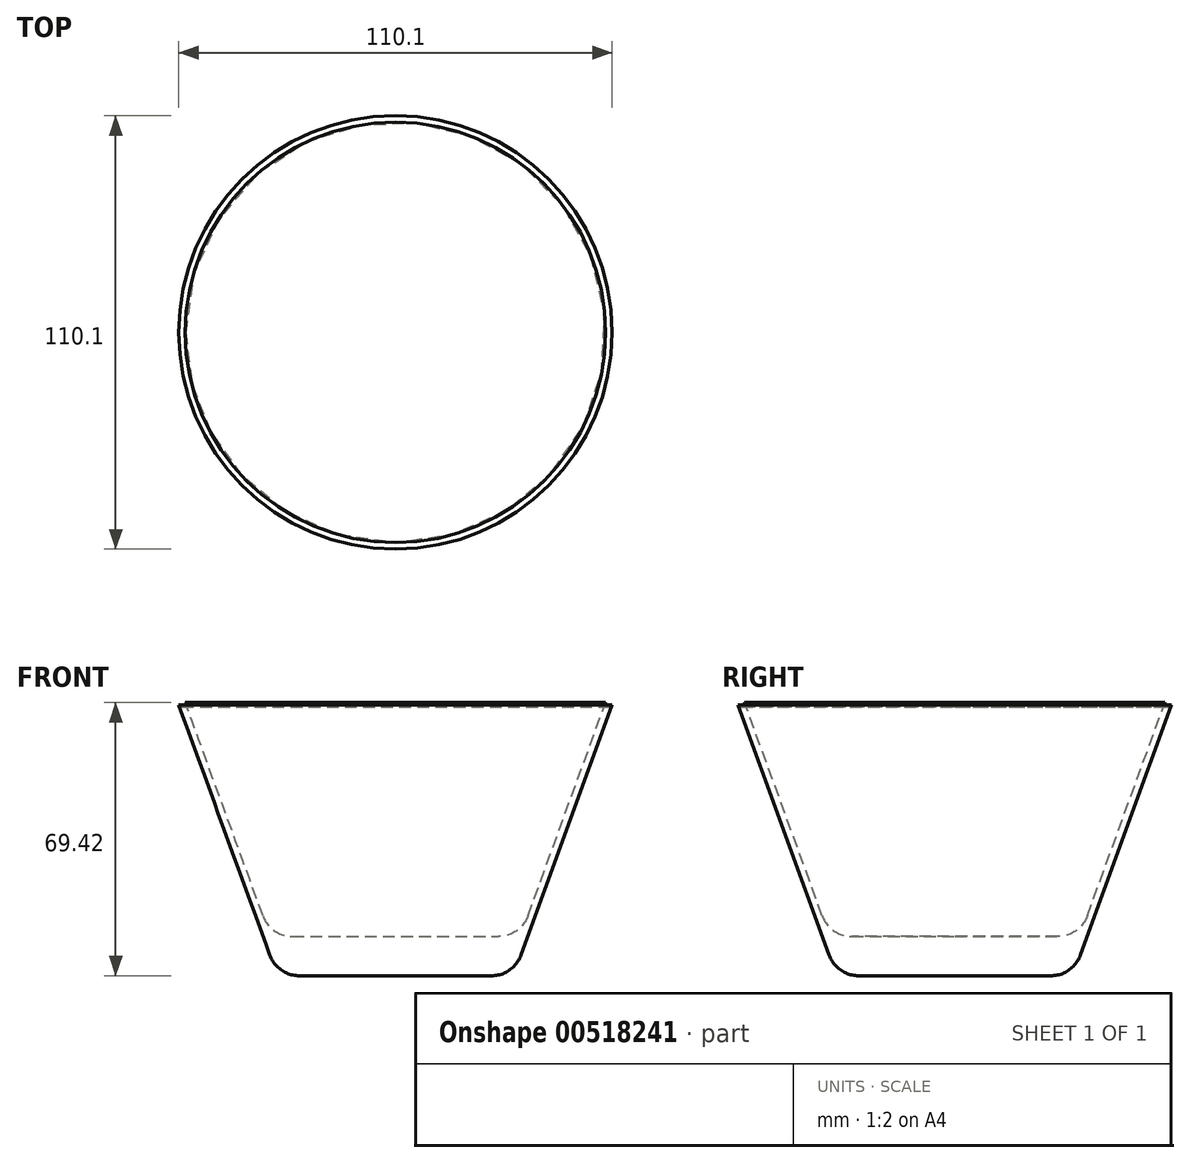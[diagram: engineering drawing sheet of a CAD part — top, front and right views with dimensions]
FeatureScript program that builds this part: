
annotation { "Feature Type Name" : "Feature", "Feature Type Description" : "" }
export const myFeature = defineFeature(function(context is Context, id is Id, definition is map)
    precondition{}
    {
        {
            var Q0;
            Q0=qCreatedBy(makeId("Front.planeOp"),FACE);
            var sketch = newSketch(context, id + "F0", { "sketchPlane" : qUnion([Q0])});
            skLineSegment(sketch, "E0", {"start": v(0, 0) * mm, "end": v(24.4, 0) * mm});
            skLineSegment(sketch, "E1", {"start": v(31.92, 5.26) * mm, "end": v(55.05, 68.83) * mm});
            skPoint(sketch, "E2.visualSharp", {"position": v(30, 0) * mm});
            skArc(sketch, "E2.filletArc", {"start": v(24.4, 0) * mm, "mid": v(28.99, 1.45) * mm, "end": v(31.92, 5.26) * mm});
            skLineSegment(sketch, "E3.0", {"start": v(33.7, 15.26) * mm, "end": v(53.4, 69.42) * mm});
            skLineSegment(sketch, "E4", {"start": v(0, 10) * mm, "end": v(26.18, 10) * mm});
            skArc(sketch, "E5.filletArc", {"start": v(26.18, 10) * mm, "mid": v(30.76, 11.45) * mm, "end": v(33.7, 15.26) * mm});
            skCircle(sketch, "E6", {"center": v(54.23, 69.12) * mm, "radius": 0.88 * mm});
            skPoint(sketch, "E6.first.point", {"position": v(53.4, 69.42) * mm});
            skPoint(sketch, "E6.second.point", {"position": v(54.23, 70) * mm});
            skPoint(sketch, "E6.third.point", {"position": v(55.05, 68.83) * mm});
            skLineSegment(sketch, "E7", {"start": v(0, 0) * mm, "end": v(0, 10) * mm});
            skLineSegment(sketch, "E8", {"start": v(0, 10) * mm, "end": v(0, 72.42) * mm, "construction": true});
            skSolve(sketch);
        }
        {
            var Q0;
            Q0=makeQuery(id+"F0.imprint","IMPRINT",FACE,{"disambiguationData":[TD([[makeQuery(id+"F0.imprint","IMPRINT",EDGE,{"derivedFrom":sQuery(id+"F0.wireOp",EDGE,"E0")}),1.0]])]});
            var Q1;
            Q1=sQuery(id+"F0.wireOp",EDGE,"E7");
            revolve(context, id + "F1", {"entities" : qUnion([Q0]), "axis" : qUnion([Q1]), "revolveType" : RevolveType.FULL});
        }
    });
